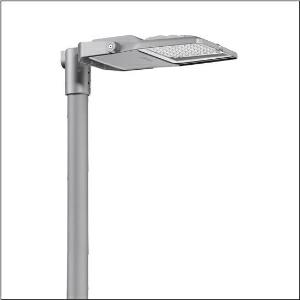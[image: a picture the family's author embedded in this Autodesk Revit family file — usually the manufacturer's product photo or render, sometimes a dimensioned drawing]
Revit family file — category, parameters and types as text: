
# Revit family: floodlight_fl_21_iq_mini___pl64_5xa7772c2e3a_d31a
name_source: partatom
category: Lighting Fixtures
units: mm (PartAtom-declared; Revit-internal decimal feet)

## family parameters
Cut with Voids When Loaded = No
Host = Face
Light Source = No
Part Type = Normal
Room Calculation Point = No
Round Connector Dimension = Use Diameter
Shared = No

## types (1)
- --- (1 x LED, 11790 lm, 87.2 W, 3000K)
    Apparent Load = 87 VA
    CIE Flux Codes = 28 80 98 100 100
    Color Rendering = 70
    Color Temperature = 3000K
    Default Elevation = 1800 mm
    Description = Floodlight FL 21 iQ mini, floodlight, primary light control with lens, of PMMA, primary optical cover: protective disc, of toughened safety glass, transparent, light distribution: PL64, light emission: direct distribution, installation type: surface-mounted, LED, High Power LED, rated luminous flux: 11.790lm, luminous efficacy: 135lm/W, light colour: 730, colour temperature: 3000K, control: Auto-Match, Temp-Guard, Night-Set, Smart-Wire, Desk-Remote (wireless, voltage-free reading and setting of iQ features in the workshop via application-optimized NFC function/RFID function), optimised constant luminous flux control (CLO 2.0), Light-Fading, Lumen-Switch, with terminal, 6-pole, mains connection: 220..240V, AC, 50/60Hz, start of lifetime: 87W, end of service life: 92W, reduction: 40W, luminaire housing, of diecast aluminium, powder-coated, Siteco® metallic grey (DB 702S), corrosivity category C5 mid according to DIN EN ISO 12944, sealing non-destructively replaceable, please order mast flange separately, mast bracket, of steel, galvanised, powder-coated, protection rating (complete): IP66, insulation class (complete): insulation class II (safety insulation), certification: CE, ENEC, VDE, protection symbol: D, impact resistance: IK08, permissible operating ambient temperature: -40..+40°C, permissible operating ambient temperature for outdoor applications: -40..+50°C, standard: DIN EN 12944, LABS conformity tested according to VDMA 24364:2018-05, packaging unit: 1 piece

Light Distribution: PL64
    Height = 70 mm
    Lamp = 1 x LED
    Lamp Light Flux = 11790 lm
    Lamp Power = 87.2 W
    Lamp count = 1
    Length = 485 mm
    Luminous efficacy = 135 lm/W
    Manufacturer = Siteco
    ModVariant = No
    Model = 5XA7772C2E3A
    Number of Poles = 1
    OnlyDefault = Yes
    Power Factor = 1
    Product Name = Floodlight FL 21 iQ mini | PL64
    Product group = floodlight | pylon annexe
    ProductGroupID = 6200
    Protection Class = Protection class II
    Protection Degree = IP 66
    RLX_Detail_Level = 1
    RLX_Emergency_Light_Flux = 0 lm
    RLX_Emergency_Type = 0
    RLX_Emergency_Type_DB = No
    RlxData = <blob elided: 101377 chars, md5=8c1bbcdc>
    Socket = socket
    Standby Power = 0 W
    System Light Flux = 11790 lm
    System Power = 87 W
    Type Comments = factory setting: luminous flux: 100 % | dim-lin: 254 | 456 mA
    Type Image = l_1007125.jpg
    URL = http://relux.com
    VarID = @adj_098661
    Voltage = 0 V
    Weight = 0.00 kg
    Width = 337 mm

## geometry (parser evidence)
native form markers: Blend x4, Sweep x13
no freeform markers — native parametric forms only
